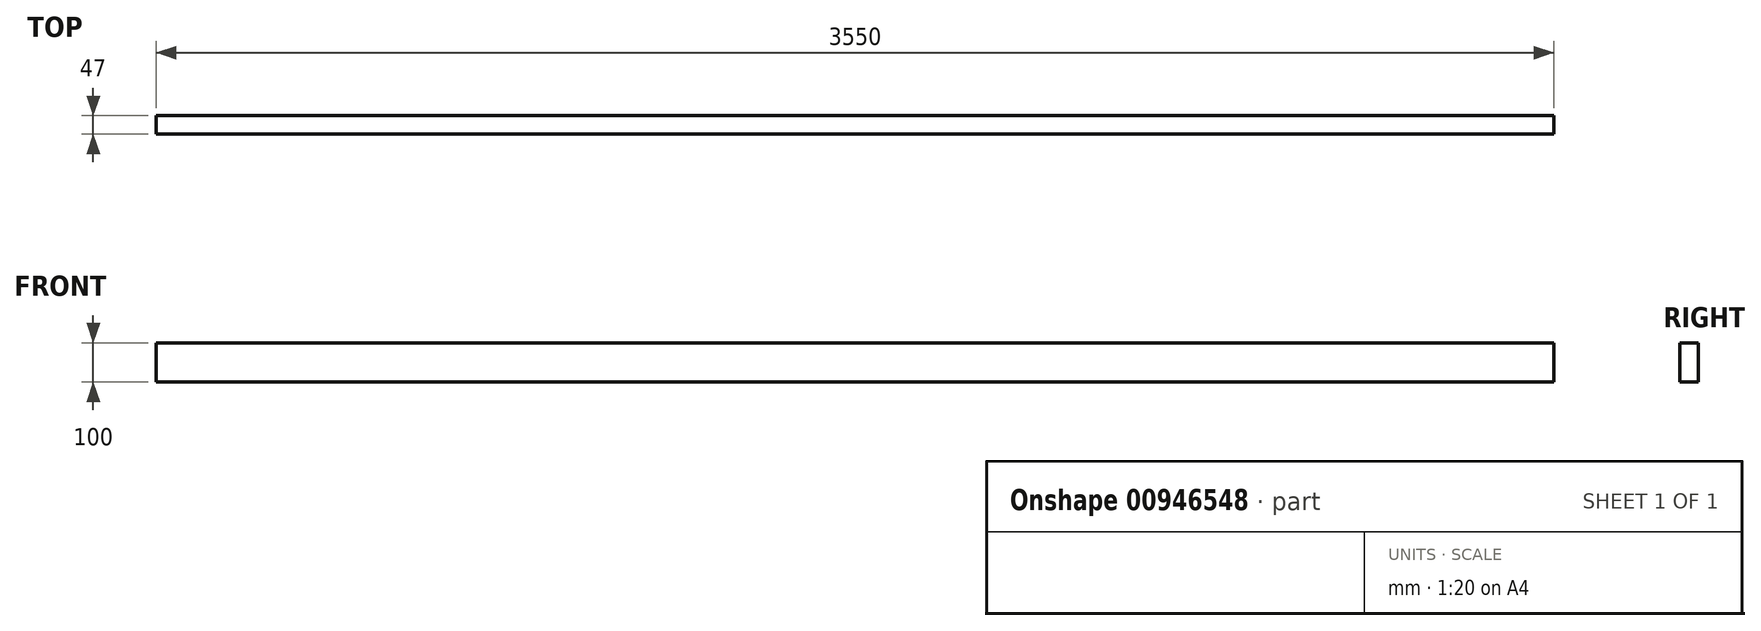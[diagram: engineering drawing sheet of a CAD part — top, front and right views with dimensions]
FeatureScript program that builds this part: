
annotation { "Feature Type Name" : "Feature", "Feature Type Description" : "" }
export const myFeature = defineFeature(function(context is Context, id is Id, definition is map)
    precondition{}
    {
        {
            var Q0;
            Q0=qCreatedBy(makeId("Right.planeOp"),FACE);
            var sketch = newSketch(context, id + "F0", { "sketchPlane" : qUnion([Q0])});
            skLineSegment(sketch, "E0.bottom", {"start": v(0, 0) * mm, "end": v(-47, 0) * mm});
            skLineSegment(sketch, "E0.top", {"start": v(0, 100) * mm, "end": v(-47, 100) * mm});
            skLineSegment(sketch, "E0.left", {"start": v(0, 0) * mm, "end": v(0, 100) * mm});
            skLineSegment(sketch, "E0.right", {"start": v(-47, 0) * mm, "end": v(-47, 100) * mm});
            skSolve(sketch);
        }
        {
            var Q0;
            Q0=qSketchRegion(id+"F0",true);
            extrude(context, id + "F1", {"entities" : qUnion([Q0]), "depth" : 3550 * mm, "offsetDistance" : 25 * mm});
        }
    });
